# Revit family: IRL-T16-R1X145-45xx-W
name_source: partatom
category: Leuchten
revit_build: Autodesk Revit 2017 (Build: 20190508_0315(x64)
units: mm (PartAtom-declared; Revit-internal decimal feet)

## family parameters
Basisbauteil = Fläche
Beim Laden mit Abzugskörper schneiden = Nein
Bemaßung runder Anschluss = Durchmesser verwenden
Gemeinsam genutzt = Nein
Lichtquelle = Ja
OmniClass-Nummer = 23.80.70.11
OmniClass-Titel = Luminaries for Internal Lighting
Raumberechnungspunkt = Nein
Teiletyp = Normal

## types (1)
- IRL-T16-R1X145/45xx-W
    Baugruppenkennzeichen = D5020200
    Datei für fotometrisches Netz = IRL-T16-R1x145.IES
    Emissionsform beim Rendern sichtbar = Nein
    Farbfilter = 16777215
    Farbtemperaturverschiebung bei Dämpfen der Lampe = <Keine Auswahl>
    Hersteller = RIDI Leuchten GmbH
    Lampe = LED
    Modell = 0950084
    Neigungswinkel = 90.00°
    Scheinlast = 45 VA
    URL = www.ridi.de
    Von Breite des Rechtecks ausssenden = 1700 mm  [stored 5.57743 ft]
    Von Länge des Rechtecks aussenden = 65 mm  [stored 0.213255 ft]
    Vorgabe-Ansicht = 0 mm  [stored 0 ft]
    brand = RIDI
    conformity mark = CE
    electrical safety class = 1
    height = 91 mm  [stored 0.298556 ft]
    ingress protection (IP) code = IP 66/IP 68+69K
    length = 1790 mm  [stored 5.8727 ft]
    nominal frequency = 50-60Hz
    nominal voltage = 230
    product name = IRL-T16-R1X145/45xx-W
    rated input power = 45
    voltage type (AC, DC, UC) = AC
    weight = 2,5 kg
    width = 91 mm  [stored 0.298556 ft]

note: [stored X ft] marks values corroborated as IEEE doubles in the binary element streams (Revit-internal decimal feet)
